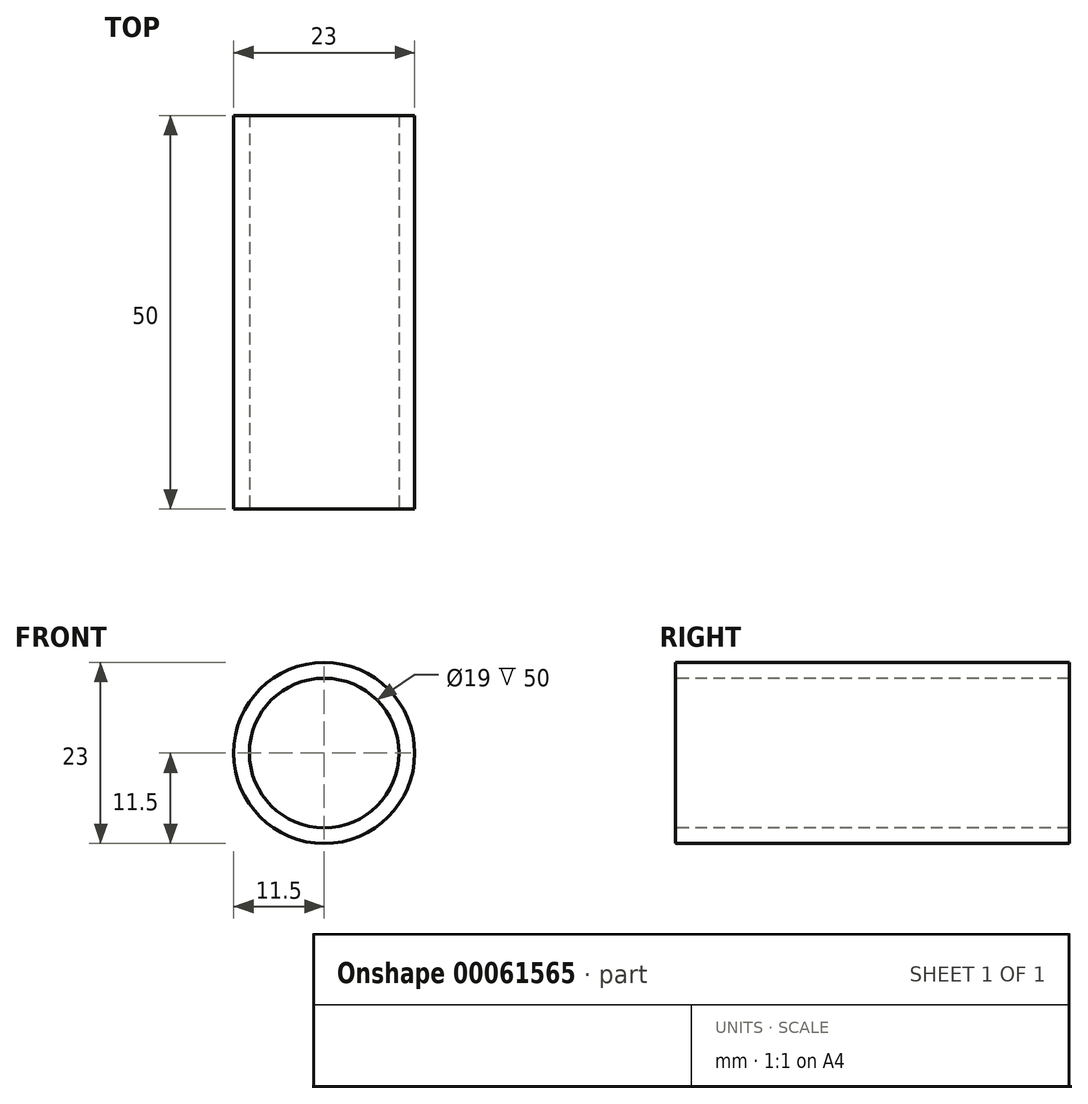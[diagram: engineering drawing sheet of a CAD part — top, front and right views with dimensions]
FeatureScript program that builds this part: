
annotation { "Feature Type Name" : "Feature", "Feature Type Description" : "" }
export const myFeature = defineFeature(function(context is Context, id is Id, definition is map)
    precondition{}
    {
        {
            var Q0;
            Q0=qCreatedBy(makeId("Front.planeOp"),FACE);
            var sketch = newSketch(context, id + "F0", { "sketchPlane" : qUnion([Q0])});
            skCircle(sketch, "E0", {"center": v(0, 0) * mm, "radius": 11.5 * mm});
            skCircle(sketch, "E1", {"center": v(0, 0) * mm, "radius": 9.5 * mm});
            skSolve(sketch);
        }
        {
            var Q0;
            Q0 = qSketchRegion(id + "F0", true);
            extrude(context, id + "F1", {"entities" : qUnion([Q0]), "oppositeDirection" : true, "depth" : 50 * mm});
        }
    });
